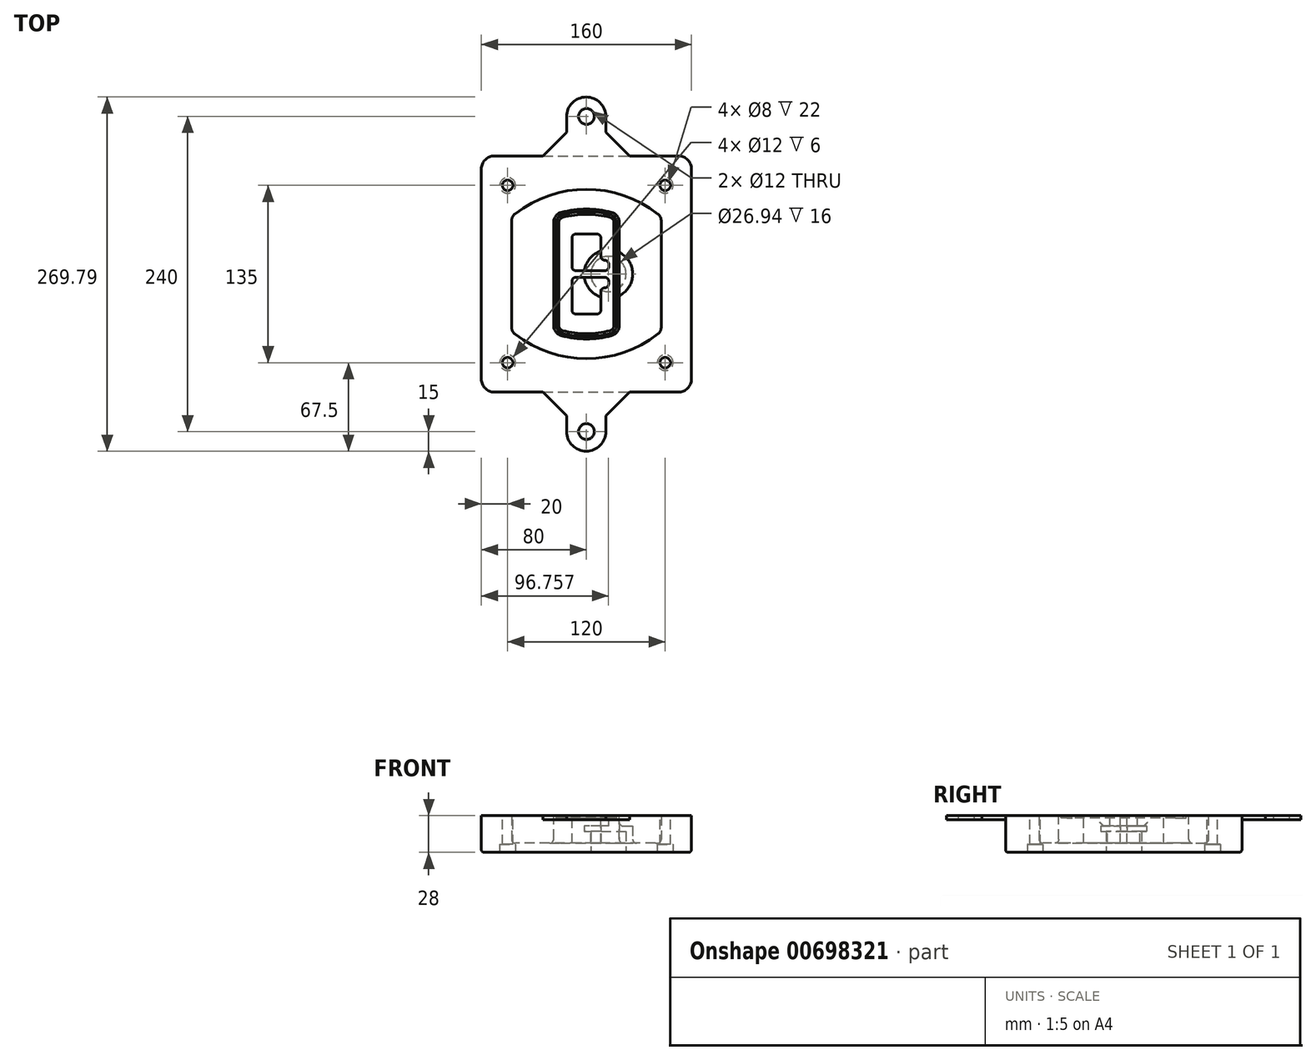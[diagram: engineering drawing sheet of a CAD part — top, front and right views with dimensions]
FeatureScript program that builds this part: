
annotation { "Feature Type Name" : "Feature", "Feature Type Description" : "" }
export const myFeature = defineFeature(function(context is Context, id is Id, definition is map)
    precondition{}
    {
        {
            var Q0;
            Q0=qCreatedBy(makeId("Top.planeOp"),FACE);
            var sketch = newSketch(context, id + "F0", { "sketchPlane" : qUnion([Q0])});
            skPoint(sketch, "E0.rect.middle", {"position": v(0, 0) * mm});
            skLineSegment(sketch, "E1.bottom", {"start": v(-70, -90) * mm, "end": v(70, -90) * mm});
            skLineSegment(sketch, "E1.top", {"start": v(-70, 90) * mm, "end": v(70, 90) * mm});
            skLineSegment(sketch, "E1.left", {"start": v(-80, -80) * mm, "end": v(-80, 80) * mm});
            skLineSegment(sketch, "E1.right", {"start": v(80, -80) * mm, "end": v(80, 80) * mm});
            skLineSegment(sketch, "E2", {"start": v(-80, 90) * mm, "end": v(80, -90) * mm, "construction": true});
            skLineSegment(sketch, "E3", {"start": v(80, 90) * mm, "end": v(-80, -90) * mm, "construction": true});
            skCircle(sketch, "E4", {"center": v(-60, 67.5) * mm, "radius": 4 * mm});
            skCircle(sketch, "E5", {"center": v(60, 67.5) * mm, "radius": 4 * mm});
            skCircle(sketch, "E6", {"center": v(60, -67.5) * mm, "radius": 4 * mm});
            skCircle(sketch, "E7", {"center": v(-60, -67.5) * mm, "radius": 4 * mm});
            skLineSegment(sketch, "E8", {"start": v(-60, 67.5) * mm, "end": v(60, 67.5) * mm, "construction": true});
            skLineSegment(sketch, "E9", {"start": v(60, 67.5) * mm, "end": v(60, -67.5) * mm, "construction": true});
            skLineSegment(sketch, "E10", {"start": v(60, -67.5) * mm, "end": v(-60, -67.5) * mm, "construction": true});
            skLineSegment(sketch, "E11", {"start": v(-60, -67.5) * mm, "end": v(-60, 67.5) * mm, "construction": true});
            skLineSegment(sketch, "E12", {"start": v(-60, 40.3) * mm, "end": v(-60, -40.3) * mm});
            skLineSegment(sketch, "E13", {"start": v(60, 40.3) * mm, "end": v(60, -40.3) * mm});
            skArc(sketch, "E14", {"start": v(56.15, 48.18) * mm, "mid": v(0, 67.5) * mm, "end": v(-56.15, 48.18) * mm});
            skArc(sketch, "E15", {"start": v(-56.15, -48.18) * mm, "mid": v(0, -67.5) * mm, "end": v(56.15, -48.18) * mm});
            skLineSegment(sketch, "E16", {"start": v(-60, 0) * mm, "end": v(60, 0) * mm, "construction": true});
            skPoint(sketch, "E17.visualSharp", {"position": v(-60, -45) * mm});
            skArc(sketch, "E17.filletArc", {"start": v(-60, -40.3) * mm, "mid": v(-58.99, -44.68) * mm, "end": v(-56.15, -48.18) * mm});
            skPoint(sketch, "E18.visualSharp", {"position": v(-60, 45) * mm});
            skArc(sketch, "E18.filletArc", {"start": v(-56.15, 48.18) * mm, "mid": v(-58.99, 44.68) * mm, "end": v(-60, 40.3) * mm});
            skPoint(sketch, "E19.visualSharp", {"position": v(60, 45) * mm});
            skArc(sketch, "E19.filletArc", {"start": v(60, 40.3) * mm, "mid": v(58.99, 44.68) * mm, "end": v(56.15, 48.18) * mm});
            skPoint(sketch, "E20.visualSharp", {"position": v(60, -45) * mm});
            skArc(sketch, "E20.filletArc", {"start": v(56.15, -48.18) * mm, "mid": v(58.99, -44.68) * mm, "end": v(60, -40.3) * mm});
            skPoint(sketch, "E21.visualSharp", {"position": v(-80, 90) * mm});
            skArc(sketch, "E21.filletArc", {"start": v(-70, 90) * mm, "mid": v(-77.07, 87.07) * mm, "end": v(-80, 80) * mm});
            skPoint(sketch, "E22.visualSharp", {"position": v(80, 90) * mm});
            skArc(sketch, "E22.filletArc", {"start": v(80, 80) * mm, "mid": v(77.07, 87.07) * mm, "end": v(70, 90) * mm});
            skPoint(sketch, "E23.visualSharp", {"position": v(80, -90) * mm});
            skArc(sketch, "E23.filletArc", {"start": v(70, -90) * mm, "mid": v(77.07, -87.07) * mm, "end": v(80, -80) * mm});
            skPoint(sketch, "E24.visualSharp", {"position": v(-80, -90) * mm});
            skArc(sketch, "E24.filletArc", {"start": v(-80, -80) * mm, "mid": v(-77.07, -87.07) * mm, "end": v(-70, -90) * mm});
            skArc(sketch, "E25.0", {"start": v(57, 40.3) * mm, "mid": v(56.3, 43.36) * mm, "end": v(54.3, 45.81) * mm});
            skLineSegment(sketch, "E25.1", {"start": v(57, 40.3) * mm, "end": v(57, -40.3) * mm});
            skArc(sketch, "E25.2", {"start": v(54.3, -45.81) * mm, "mid": v(56.3, -43.36) * mm, "end": v(57, -40.3) * mm});
            skArc(sketch, "E25.3", {"start": v(-54.3, -45.81) * mm, "mid": v(0, -64.5) * mm, "end": v(54.3, -45.81) * mm});
            skArc(sketch, "E25.4", {"start": v(-57, -40.3) * mm, "mid": v(-56.3, -43.36) * mm, "end": v(-54.3, -45.81) * mm});
            skArc(sketch, "E25.5", {"start": v(54.3, 45.81) * mm, "mid": v(0, 64.5) * mm, "end": v(-54.3, 45.81) * mm});
            skLineSegment(sketch, "E25.6", {"start": v(-57, 40.3) * mm, "end": v(-57, -40.3) * mm});
            skArc(sketch, "E25.7", {"start": v(-54.3, 45.81) * mm, "mid": v(-56.3, 43.36) * mm, "end": v(-57, 40.3) * mm});
            skArc(sketch, "E26.0", {"start": v(-58.62, 51.33) * mm, "mid": v(-62.58, 46.43) * mm, "end": v(-64, 40.3) * mm});
            skArc(sketch, "E26.1", {"start": v(58.62, 51.33) * mm, "mid": v(0, 71.5) * mm, "end": v(-58.62, 51.33) * mm});
            skArc(sketch, "E26.2", {"start": v(64, 40.3) * mm, "mid": v(62.58, 46.43) * mm, "end": v(58.62, 51.33) * mm});
            skLineSegment(sketch, "E26.3", {"start": v(64, 40.3) * mm, "end": v(64, -40.3) * mm});
            skArc(sketch, "E26.4", {"start": v(58.62, -51.33) * mm, "mid": v(62.58, -46.43) * mm, "end": v(64, -40.3) * mm});
            skLineSegment(sketch, "E26.5", {"start": v(-64, 40.3) * mm, "end": v(-64, -40.3) * mm});
            skArc(sketch, "E26.6", {"start": v(-58.62, -51.33) * mm, "mid": v(0, -71.5) * mm, "end": v(58.62, -51.33) * mm});
            skArc(sketch, "E26.7", {"start": v(-64, -40.3) * mm, "mid": v(-62.58, -46.43) * mm, "end": v(-58.62, -51.33) * mm});
            skSolve(sketch);
        }
        {
            var Q0;
            Q0=makeQuery(id+"F0.imprint","IMPRINT",FACE,{"disambiguationData":[TD([[makeQuery(id+"F0.imprint","IMPRINT",EDGE,{"derivedFrom":sQuery(id+"F0.wireOp",EDGE,"E1.bottom")}),1.0]])]});
            var Q1;
            Q1=makeQuery(id+"F0.imprint","IMPRINT",FACE,{"disambiguationData":[TD([[makeQuery(id+"F0.imprint","IMPRINT",EDGE,{"derivedFrom":sQuery(id+"F0.wireOp",EDGE,"E12")}),1.0]])]});
            var Q2;
            Q2=makeQuery(id+"F0.imprint","IMPRINT",FACE,{"disambiguationData":[TD([[makeQuery(id+"F0.imprint","IMPRINT",EDGE,{"derivedFrom":sQuery(id+"F0.wireOp",EDGE,"E25.0")}),1.0]])]});
            var Q3;
            Q3=makeQuery(id+"F0.imprint","IMPRINT",FACE,{"disambiguationData":[TD([[makeQuery(id+"F0.imprint","IMPRINT",EDGE,{"derivedFrom":sQuery(id+"F0.wireOp",EDGE,"E12")}),-1.0]])]});
            extrude(context, id + "F1", {"entities" : qUnion([Q0, Q1, Q2, Q3]), "oppositeDirection" : true, "depth" : 25 * mm, "offsetDistance" : 25 * mm});
        }
        {
            var Q0;
            Q0=makeQuery(id+"F0.imprint","IMPRINT",FACE,{"disambiguationData":[TD([[makeQuery(id+"F0.imprint","IMPRINT",EDGE,{"derivedFrom":sQuery(id+"F0.wireOp",EDGE,"E12")}),1.0]])]});
            extrude(context, id + "F2", {"entities" : qUnion([Q0]), "operationType" : NewBodyOperationType.ADD, "depth" : 3 * mm, "offsetDistance" : 25 * mm});
        }
        {
            var Q0;
            Q0=makeQuery(id+"F0.imprint","IMPRINT",FACE,{"disambiguationData":[TD([[makeQuery(id+"F0.imprint","IMPRINT",EDGE,{"derivedFrom":sQuery(id+"F0.wireOp",EDGE,"E25.0")}),1.0]])]});
            extrude(context, id + "F3", {"entities" : qUnion([Q0]), "operationType" : NewBodyOperationType.REMOVE, "oppositeDirection" : true, "depth" : 18 * mm, "offsetDistance" : 25 * mm});
        }
        {
            var Q0;
            Q0=makeQuery(id+"F2.opExtrude","CAP_FACE",FACE,{"disambiguationData":[OSD([sQuery(id+"F0.wireOp",EDGE,"E12"),sQuery(id+"F0.wireOp",EDGE,"E13"),sQuery(id+"F0.wireOp",EDGE,"E14"),sQuery(id+"F0.wireOp",EDGE,"E15"),sQuery(id+"F0.wireOp",EDGE,"E17.filletArc"),sQuery(id+"F0.wireOp",EDGE,"E18.filletArc"),sQuery(id+"F0.wireOp",EDGE,"E19.filletArc"),sQuery(id+"F0.wireOp",EDGE,"E20.filletArc"),sQuery(id+"F0.wireOp",EDGE,"E25.0"),sQuery(id+"F0.wireOp",EDGE,"E25.1"),sQuery(id+"F0.wireOp",EDGE,"E25.2"),sQuery(id+"F0.wireOp",EDGE,"E25.3"),sQuery(id+"F0.wireOp",EDGE,"E25.4"),sQuery(id+"F0.wireOp",EDGE,"E25.5"),sQuery(id+"F0.wireOp",EDGE,"E25.6"),sQuery(id+"F0.wireOp",EDGE,"E25.7")])],"isStart":false});
            var sketch = newSketch(context, id + "F4", { "sketchPlane" : qUnion([Q0])});
            skArc(sketch, "E27.0", {"start": v(-19.08, -46.97) * mm, "mid": v(0, -49.5) * mm, "end": v(19.08, -46.97) * mm});
            skArc(sketch, "E28.0", {"start": v(19.08, 46.97) * mm, "mid": v(0, 49.5) * mm, "end": v(-19.08, 46.97) * mm});
            skLineSegment(sketch, "E29", {"start": v(-25, 39.25) * mm, "end": v(-25, -39.25) * mm});
            skLineSegment(sketch, "E30", {"start": v(25, 39.25) * mm, "end": v(25, -39.25) * mm});
            skLineSegment(sketch, "E31", {"start": v(-25, 45.1) * mm, "end": v(25, 45.1) * mm, "construction": true});
            skLineSegment(sketch, "E32", {"start": v(-25, -45.1) * mm, "end": v(25, -45.1) * mm, "construction": true});
            skPoint(sketch, "E33.visualSharp", {"position": v(-25, 45.1) * mm});
            skArc(sketch, "E33.filletArc", {"start": v(-19.08, 46.97) * mm, "mid": v(-23.35, 44.11) * mm, "end": v(-25, 39.25) * mm});
            skPoint(sketch, "E34.visualSharp", {"position": v(25, 45.1) * mm});
            skArc(sketch, "E34.filletArc", {"start": v(25, 39.25) * mm, "mid": v(23.35, 44.11) * mm, "end": v(19.08, 46.97) * mm});
            skPoint(sketch, "E35.visualSharp", {"position": v(25, -45.1) * mm});
            skArc(sketch, "E35.filletArc", {"start": v(19.08, -46.97) * mm, "mid": v(23.35, -44.11) * mm, "end": v(25, -39.25) * mm});
            skPoint(sketch, "E36.visualSharp", {"position": v(-25, -45.1) * mm});
            skArc(sketch, "E36.filletArc", {"start": v(-25, -39.25) * mm, "mid": v(-23.35, -44.11) * mm, "end": v(-19.08, -46.97) * mm});
            skArc(sketch, "E37.0", {"start": v(54.3, 45.81) * mm, "mid": v(0, 64.5) * mm, "end": v(-54.3, 45.81) * mm});
            skArc(sketch, "E37.1", {"start": v(-54.3, 45.81) * mm, "mid": v(-56.3, 43.36) * mm, "end": v(-57, 40.3) * mm});
            skLineSegment(sketch, "E37.2", {"start": v(-57, 40.3) * mm, "end": v(-57, -40.3) * mm});
            skArc(sketch, "E37.3", {"start": v(-57, -40.3) * mm, "mid": v(-56.3, -43.36) * mm, "end": v(-54.3, -45.81) * mm});
            skArc(sketch, "E37.4", {"start": v(-54.3, -45.81) * mm, "mid": v(0, -64.5) * mm, "end": v(54.3, -45.81) * mm});
            skArc(sketch, "E37.5", {"start": v(54.3, -45.81) * mm, "mid": v(56.3, -43.36) * mm, "end": v(57, -40.3) * mm});
            skLineSegment(sketch, "E37.6", {"start": v(57, 40.3) * mm, "end": v(57, -40.3) * mm});
            skArc(sketch, "E37.7", {"start": v(57, 40.3) * mm, "mid": v(56.3, 43.36) * mm, "end": v(54.3, 45.81) * mm});
            skLineSegment(sketch, "E38.0", {"start": v(23, 39.25) * mm, "end": v(23, -39.25) * mm});
            skArc(sketch, "E38.1", {"start": v(18.56, -45.04) * mm, "mid": v(21.76, -42.9) * mm, "end": v(23, -39.25) * mm});
            skArc(sketch, "E38.2", {"start": v(-18.56, -45.04) * mm, "mid": v(0, -47.5) * mm, "end": v(18.56, -45.04) * mm});
            skArc(sketch, "E38.3", {"start": v(-23, -39.25) * mm, "mid": v(-21.76, -42.9) * mm, "end": v(-18.56, -45.04) * mm});
            skLineSegment(sketch, "E38.4", {"start": v(-23, 39.25) * mm, "end": v(-23, -39.25) * mm});
            skArc(sketch, "E38.5", {"start": v(23, 39.25) * mm, "mid": v(21.76, 42.9) * mm, "end": v(18.56, 45.04) * mm});
            skArc(sketch, "E38.6", {"start": v(-18.56, 45.04) * mm, "mid": v(-21.76, 42.9) * mm, "end": v(-23, 39.25) * mm});
            skArc(sketch, "E38.7", {"start": v(18.56, 45.04) * mm, "mid": v(0, 47.5) * mm, "end": v(-18.56, 45.04) * mm});
            skArc(sketch, "E39.0", {"start": v(21, 39.25) * mm, "mid": v(20.18, 41.68) * mm, "end": v(18.04, 43.1) * mm});
            skLineSegment(sketch, "E39.1", {"start": v(21, 39.25) * mm, "end": v(21, -39.25) * mm});
            skArc(sketch, "E39.2", {"start": v(18.04, -43.1) * mm, "mid": v(20.18, -41.68) * mm, "end": v(21, -39.25) * mm});
            skArc(sketch, "E39.3", {"start": v(-18.04, -43.1) * mm, "mid": v(0, -45.5) * mm, "end": v(18.04, -43.1) * mm});
            skArc(sketch, "E39.4", {"start": v(-21, -39.25) * mm, "mid": v(-20.18, -41.68) * mm, "end": v(-18.04, -43.1) * mm});
            skArc(sketch, "E39.5", {"start": v(18.04, 43.1) * mm, "mid": v(0, 45.5) * mm, "end": v(-18.04, 43.1) * mm});
            skLineSegment(sketch, "E39.6", {"start": v(-21, 39.25) * mm, "end": v(-21, -39.25) * mm});
            skArc(sketch, "E39.7", {"start": v(-18.04, 43.1) * mm, "mid": v(-20.18, 41.68) * mm, "end": v(-21, 39.25) * mm});
            skLineSegment(sketch, "E40", {"start": v(-25, 0) * mm, "end": v(25, 0) * mm, "construction": true});
            skLineSegment(sketch, "E41", {"start": v(-11, 5.5) * mm, "end": v(-11, 27.5) * mm});
            skLineSegment(sketch, "E42", {"start": v(-8, 30.5) * mm, "end": v(8, 30.5) * mm});
            skLineSegment(sketch, "E43", {"start": v(11, 27.5) * mm, "end": v(11, 13.5) * mm});
            skLineSegment(sketch, "E44", {"start": v(14, 10.5) * mm, "end": v(14, 10.5) * mm});
            skLineSegment(sketch, "E45", {"start": v(17, 7.5) * mm, "end": v(17, 5.5) * mm});
            skLineSegment(sketch, "E46", {"start": v(14, 2.5) * mm, "end": v(-8, 2.5) * mm});
            skPoint(sketch, "E47.visualSharp", {"position": v(-11, 30.5) * mm});
            skArc(sketch, "E47.filletArc", {"start": v(-8, 30.5) * mm, "mid": v(-10.12, 29.62) * mm, "end": v(-11, 27.5) * mm});
            skPoint(sketch, "E48.visualSharp", {"position": v(11, 30.5) * mm});
            skArc(sketch, "E48.filletArc", {"start": v(11, 27.5) * mm, "mid": v(10.12, 29.62) * mm, "end": v(8, 30.5) * mm});
            skPoint(sketch, "E49.visualSharp", {"position": v(11, 10.5) * mm});
            skArc(sketch, "E49.filletArc", {"start": v(11, 13.5) * mm, "mid": v(11.88, 11.38) * mm, "end": v(14, 10.5) * mm});
            skPoint(sketch, "E50.visualSharp", {"position": v(17, 10.5) * mm});
            skArc(sketch, "E50.filletArc", {"start": v(17, 7.5) * mm, "mid": v(16.12, 9.62) * mm, "end": v(14, 10.5) * mm});
            skPoint(sketch, "E51.visualSharp", {"position": v(17, 2.5) * mm});
            skArc(sketch, "E51.filletArc", {"start": v(14, 2.5) * mm, "mid": v(16.12, 3.38) * mm, "end": v(17, 5.5) * mm});
            skPoint(sketch, "E52.visualSharp", {"position": v(-11, 2.5) * mm});
            skArc(sketch, "E52.filletArc", {"start": v(-11, 5.5) * mm, "mid": v(-10.12, 3.38) * mm, "end": v(-8, 2.5) * mm});
            skLineSegment(sketch, "E53.0.MirrorCS", {"start": v(14, -2.5) * mm, "end": v(-8, -2.5) * mm});
            skArc(sketch, "E54.0.MirrorCS", {"start": v(-11, -5.5) * mm, "mid": v(-10.12, -3.38) * mm, "end": v(-8, -2.5) * mm});
            skLineSegment(sketch, "E55.0.MirrorCS", {"start": v(-11, -5.5) * mm, "end": v(-11, -27.5) * mm});
            skArc(sketch, "E56.0.MirrorCS", {"start": v(-8, -30.5) * mm, "mid": v(-10.12, -29.62) * mm, "end": v(-11, -27.5) * mm});
            skLineSegment(sketch, "E57.0.MirrorCS", {"start": v(-8, -30.5) * mm, "end": v(8, -30.5) * mm});
            skArc(sketch, "E58.0.MirrorCS", {"start": v(11, -27.5) * mm, "mid": v(10.12, -29.62) * mm, "end": v(8, -30.5) * mm});
            skLineSegment(sketch, "E59.0.MirrorCS", {"start": v(11, -27.5) * mm, "end": v(11, -13.5) * mm});
            skArc(sketch, "E60.0.MirrorCS", {"start": v(11, -13.5) * mm, "mid": v(11.88, -11.38) * mm, "end": v(14, -10.5) * mm});
            skArc(sketch, "E61.0.MirrorCS", {"start": v(17, -7.5) * mm, "mid": v(16.12, -9.62) * mm, "end": v(14, -10.5) * mm});
            skLineSegment(sketch, "E62.0.MirrorCS", {"start": v(17, -7.5) * mm, "end": v(17, -5.5) * mm});
            skArc(sketch, "E63.0.MirrorCS", {"start": v(14, -2.5) * mm, "mid": v(16.12, -3.38) * mm, "end": v(17, -5.5) * mm});
            skSolve(sketch);
        }
        {
            var Q0;
            Q0=makeQuery(id+"F4.imprint","IMPRINT",FACE,{"disambiguationData":[TD([[makeQuery(id+"F4.imprint","IMPRINT",EDGE,{"derivedFrom":sQuery(id+"F4.wireOp",EDGE,"E27.0")}),1.0]])]});
            var Q1;
            Q1=makeQuery(id+"F4.imprint","IMPRINT",FACE,{"disambiguationData":[TD([[makeQuery(id+"F4.imprint","IMPRINT",EDGE,{"derivedFrom":sQuery(id+"F4.wireOp",EDGE,"E38.0")}),-1.0]])]});
            var Q2;
            Q2=makeQuery(id+"F4.imprint","IMPRINT",FACE,{"disambiguationData":[TD([[makeQuery(id+"F4.imprint","IMPRINT",EDGE,{"derivedFrom":sQuery(id+"F4.wireOp",EDGE,"E39.0")}),1.0]])]});
            extrude(context, id + "F5", {"entities" : qUnion([Q0, Q1, Q2]), "operationType" : NewBodyOperationType.ADD, "endBound" : BoundingType.UP_TO_NEXT, "oppositeDirection" : true, "depth" : 25 * mm, "offsetDistance" : 25 * mm});
        }
        {
            var Q0;
            Q0=makeQuery(id+"F4.imprint","IMPRINT",FACE,{"disambiguationData":[TD([[makeQuery(id+"F4.imprint","IMPRINT",EDGE,{"derivedFrom":sQuery(id+"F4.wireOp",EDGE,"E38.0")}),-1.0]])]});
            extrude(context, id + "F6", {"entities" : qUnion([Q0]), "operationType" : NewBodyOperationType.REMOVE, "oppositeDirection" : true, "depth" : 2 * mm, "offsetDistance" : 25 * mm});
        }
        {
            var Q0;
            Q0=makeQuery(id+"F1.opExtrude","CAP_FACE",FACE,{"disambiguationData":[OSD([sQuery(id+"F0.wireOp",EDGE,"E1.bottom"),sQuery(id+"F0.wireOp",EDGE,"E1.top"),sQuery(id+"F0.wireOp",EDGE,"E1.left"),sQuery(id+"F0.wireOp",EDGE,"E1.right"),sQuery(id+"F0.wireOp",EDGE,"E4"),sQuery(id+"F0.wireOp",EDGE,"E5"),sQuery(id+"F0.wireOp",EDGE,"E6"),sQuery(id+"F0.wireOp",EDGE,"E7"),sQuery(id+"F0.wireOp",EDGE,"E21.filletArc"),sQuery(id+"F0.wireOp",EDGE,"E22.filletArc"),sQuery(id+"F0.wireOp",EDGE,"E23.filletArc"),sQuery(id+"F0.wireOp",EDGE,"E24.filletArc")])],"isStart":false});
            var sketch = newSketch(context, id + "F7", { "sketchPlane" : qUnion([Q0])});
            skCircle(sketch, "E64", {"center": v(16.76, 0) * mm, "radius": 13.47 * mm});
            skCircle(sketch, "E65", {"center": v(-45.56, 0) * mm, "radius": 13.47 * mm});
            skLineSegment(sketch, "E66", {"start": v(80, 0) * mm, "end": v(-80, 0) * mm});
            skCircle(sketch, "E67", {"center": v(16.76, 0) * mm, "radius": 18.47 * mm});
            skCircle(sketch, "E68", {"center": v(60, -67.5) * mm, "radius": 6 * mm});
            skCircle(sketch, "E69", {"center": v(-60, -67.5) * mm, "radius": 6 * mm});
            skCircle(sketch, "E70", {"center": v(-60, 67.5) * mm, "radius": 6 * mm});
            skCircle(sketch, "E71", {"center": v(60, 67.5) * mm, "radius": 6 * mm});
            skSolve(sketch);
        }
        {
            var Q0;
            {var subQ1=sQuery(id+"F7.wireOp",EDGE,"E66");var subQ4=sQuery(id+"F7.wireOp",EDGE,"E64");var subQ6=makeQuery(id+"F7.imprint","INTERSECT",VERTEX,{"disambiguationData":[OD(0.0)],"derivedFrom":[subQ4,subQ1]});Q0=makeQuery(id+"F7.imprint","IMPRINT",FACE,{"disambiguationData":[TD([[makeQuery(id+"F7.imprint","IMPRINT",EDGE,{"disambiguationData":[TD([[subQ6,-1.0]])],"derivedFrom":subQ4}),-1.0]])]});}
            var Q1;
            {var subQ0=sQuery(id+"F7.wireOp",EDGE,"E66");var subQ1=sQuery(id+"F7.wireOp",EDGE,"E64");var subQ3=makeQuery(id+"F7.imprint","INTERSECT",VERTEX,{"disambiguationData":[OD(0.0)],"derivedFrom":[subQ1,subQ0]});Q1=makeQuery(id+"F7.imprint","IMPRINT",FACE,{"disambiguationData":[TD([[makeQuery(id+"F7.imprint","IMPRINT",EDGE,{"disambiguationData":[TD([[subQ3,-1.0]])],"derivedFrom":subQ1}),1.0]])]});}
            var Q2;
            {var subQ0=sQuery(id+"F7.wireOp",EDGE,"E66");var subQ1=sQuery(id+"F7.wireOp",EDGE,"E64");var subQ3=makeQuery(id+"F7.imprint","INTERSECT",VERTEX,{"disambiguationData":[OD(0.0)],"derivedFrom":[subQ1,subQ0]});Q2=makeQuery(id+"F7.imprint","IMPRINT",FACE,{"disambiguationData":[TD([[makeQuery(id+"F7.imprint","IMPRINT",EDGE,{"disambiguationData":[TD([[subQ3,1.0]])],"derivedFrom":subQ1}),1.0]])]});}
            var Q3;
            {var subQ1=sQuery(id+"F7.wireOp",EDGE,"E66");var subQ4=sQuery(id+"F7.wireOp",EDGE,"E64");var subQ6=makeQuery(id+"F7.imprint","INTERSECT",VERTEX,{"disambiguationData":[OD(0.0)],"derivedFrom":[subQ4,subQ1]});Q3=makeQuery(id+"F7.imprint","IMPRINT",FACE,{"disambiguationData":[TD([[makeQuery(id+"F7.imprint","IMPRINT",EDGE,{"disambiguationData":[TD([[subQ6,1.0]])],"derivedFrom":subQ4}),-1.0]])]});}
            extrude(context, id + "F8", {"entities" : qUnion([Q0, Q1, Q2, Q3]), "operationType" : NewBodyOperationType.ADD, "oppositeDirection" : true, "depth" : 20 * mm, "offsetDistance" : 25 * mm});
        }
        {
            var Q0;
            {var subQ0=sQuery(id+"F7.wireOp",EDGE,"E66");var subQ1=sQuery(id+"F7.wireOp",EDGE,"E64");var subQ3=makeQuery(id+"F7.imprint","INTERSECT",VERTEX,{"disambiguationData":[OD(0.0)],"derivedFrom":[subQ1,subQ0]});Q0=makeQuery(id+"F7.imprint","IMPRINT",FACE,{"disambiguationData":[TD([[makeQuery(id+"F7.imprint","IMPRINT",EDGE,{"disambiguationData":[TD([[subQ3,-1.0]])],"derivedFrom":subQ1}),1.0]])]});}
            var Q1;
            {var subQ0=sQuery(id+"F7.wireOp",EDGE,"E66");var subQ1=sQuery(id+"F7.wireOp",EDGE,"E64");var subQ3=makeQuery(id+"F7.imprint","INTERSECT",VERTEX,{"disambiguationData":[OD(0.0)],"derivedFrom":[subQ1,subQ0]});Q1=makeQuery(id+"F7.imprint","IMPRINT",FACE,{"disambiguationData":[TD([[makeQuery(id+"F7.imprint","IMPRINT",EDGE,{"disambiguationData":[TD([[subQ3,1.0]])],"derivedFrom":subQ1}),1.0]])]});}
            extrude(context, id + "F9", {"entities" : qUnion([Q0, Q1]), "operationType" : NewBodyOperationType.REMOVE, "oppositeDirection" : true, "depth" : 16 * mm, "offsetDistance" : 25 * mm});
        }
        {
            var Q0;
            Q0=makeQuery(id+"F7.imprint","IMPRINT",FACE,{"disambiguationData":[TD([[makeQuery(id+"F7.imprint","IMPRINT",EDGE,{"derivedFrom":sQuery(id+"F7.wireOp",EDGE,"E68")}),1.0]])]});
            var Q1;
            Q1=makeQuery(id+"F7.imprint","IMPRINT",FACE,{"disambiguationData":[TD([[makeQuery(id+"F7.imprint","IMPRINT",EDGE,{"derivedFrom":makeQuery(id+"F1.opExtrude","CAP_EDGE",EDGE,{"disambiguationData":[OSD([sQuery(id+"F0.wireOp",EDGE,"E5")])],"isStart":false})}),-1.0]])]});
            var Q2;
            Q2=makeQuery(id+"F7.imprint","IMPRINT",FACE,{"disambiguationData":[TD([[makeQuery(id+"F7.imprint","IMPRINT",EDGE,{"derivedFrom":sQuery(id+"F7.wireOp",EDGE,"E69")}),1.0]])]});
            var Q3;
            Q3=makeQuery(id+"F7.imprint","IMPRINT",FACE,{"disambiguationData":[TD([[makeQuery(id+"F7.imprint","IMPRINT",EDGE,{"derivedFrom":makeQuery(id+"F1.opExtrude","CAP_EDGE",EDGE,{"disambiguationData":[OSD([sQuery(id+"F0.wireOp",EDGE,"E4")])],"isStart":false})}),-1.0]])]});
            var Q4;
            Q4=makeQuery(id+"F7.imprint","IMPRINT",FACE,{"disambiguationData":[TD([[makeQuery(id+"F7.imprint","IMPRINT",EDGE,{"derivedFrom":sQuery(id+"F7.wireOp",EDGE,"E70")}),1.0]])]});
            var Q5;
            Q5=makeQuery(id+"F7.imprint","IMPRINT",FACE,{"disambiguationData":[TD([[makeQuery(id+"F7.imprint","IMPRINT",EDGE,{"derivedFrom":makeQuery(id+"F1.opExtrude","CAP_EDGE",EDGE,{"disambiguationData":[OSD([sQuery(id+"F0.wireOp",EDGE,"E7")])],"isStart":false})}),-1.0]])]});
            var Q6;
            Q6=makeQuery(id+"F7.imprint","IMPRINT",FACE,{"disambiguationData":[TD([[makeQuery(id+"F7.imprint","IMPRINT",EDGE,{"derivedFrom":sQuery(id+"F7.wireOp",EDGE,"E71")}),1.0]])]});
            var Q7;
            Q7=makeQuery(id+"F7.imprint","IMPRINT",FACE,{"disambiguationData":[TD([[makeQuery(id+"F7.imprint","IMPRINT",EDGE,{"derivedFrom":makeQuery(id+"F1.opExtrude","CAP_EDGE",EDGE,{"disambiguationData":[OSD([sQuery(id+"F0.wireOp",EDGE,"E6")])],"isStart":false})}),-1.0]])]});
            extrude(context, id + "F10", {"entities" : qUnion([Q0, Q1, Q2, Q3, Q4, Q5, Q6, Q7]), "operationType" : NewBodyOperationType.REMOVE, "oppositeDirection" : true, "depth" : 6 * mm, "offsetDistance" : 25 * mm});
        }
        {
            var Q0;
            Q0=makeQuery(id+"F9.boolean.opBoolean","COPY",FACE,{"derivedFrom":makeQuery(id+"F9.opExtrude","CAP_FACE",FACE,{"disambiguationData":[OSD([sQuery(id+"F7.wireOp",EDGE,"E64")])],"isStart":false})});
            var sketch = newSketch(context, id + "F11", { "sketchPlane" : qUnion([Q0])});
            skArc(sketch, "E72.0", {"start": v(11, 17.55) * mm, "mid": v(2.57, 11.82) * mm, "end": v(-1.54, 2.5) * mm});
            skArc(sketch, "E72.1", {"start": v(-1.54, -2.5) * mm, "mid": v(2.57, -11.82) * mm, "end": v(11, -17.55) * mm});
            skLineSegment(sketch, "E73", {"start": v(-1.54, -2.5) * mm, "end": v(14, -2.5) * mm});
            skLineSegment(sketch, "E74.0", {"start": v(14, 2.5) * mm, "end": v(-1.54, 2.5) * mm});
            skArc(sketch, "E74.1", {"start": v(14, 2.5) * mm, "mid": v(16.12, 3.38) * mm, "end": v(17, 5.5) * mm});
            skLineSegment(sketch, "E74.2", {"start": v(17, 7.5) * mm, "end": v(17, 5.5) * mm});
            skArc(sketch, "E74.3", {"start": v(17, 7.5) * mm, "mid": v(16.12, 9.62) * mm, "end": v(14, 10.5) * mm});
            skArc(sketch, "E74.4", {"start": v(11, 13.5) * mm, "mid": v(11.88, 11.38) * mm, "end": v(14, 10.5) * mm});
            skLineSegment(sketch, "E74.5", {"start": v(11, 17.55) * mm, "end": v(11, 13.5) * mm});
            skLineSegment(sketch, "E74.7", {"start": v(14, -2.5) * mm, "end": v(-1.54, -2.5) * mm});
            skArc(sketch, "E74.8", {"start": v(14, -2.5) * mm, "mid": v(16.12, -3.38) * mm, "end": v(17, -5.5) * mm});
            skLineSegment(sketch, "E74.9", {"start": v(17, -7.5) * mm, "end": v(17, -5.5) * mm});
            skArc(sketch, "E74.10", {"start": v(17, -7.5) * mm, "mid": v(16.12, -9.62) * mm, "end": v(14, -10.5) * mm});
            skArc(sketch, "E74.11", {"start": v(11, -13.5) * mm, "mid": v(11.88, -11.38) * mm, "end": v(14, -10.5) * mm});
            skLineSegment(sketch, "E74.12", {"start": v(11, -17.55) * mm, "end": v(11, -13.5) * mm});
            skPoint(sketch, "E75.orphan", {"position": v(11, -27.5) * mm});
            skPoint(sketch, "E76.orphan", {"position": v(-8, -2.5) * mm});
            skPoint(sketch, "E77.orphan", {"position": v(-8, 2.5) * mm});
            skPoint(sketch, "E78.orphan", {"position": v(11, 27.5) * mm});
            skSolve(sketch);
        }
        {
            var Q0;
            {var subQ7=sQuery(id+"F11.wireOp",EDGE,"E72.0");var subQ14=sQuery(id+"F11.wireOp",EDGE,"E72.1");var subQ16=sQuery(id+"F11.wireOp",EDGE,"E74.1");var subQ18=sQuery(id+"F11.wireOp",EDGE,"E74.8");Q0=qUnion([makeQuery(id+"F11.imprint","IMPRINT",FACE,{"disambiguationData":[TD([[makeQuery(id+"F11.imprint","IMPRINT",EDGE,{"derivedFrom":subQ7}),1.0]])]}),makeQuery(id+"F11.imprint","IMPRINT",FACE,{"disambiguationData":[TD([[makeQuery(id+"F11.imprint","IMPRINT",EDGE,{"derivedFrom":subQ14}),1.0]])]}),makeQuery(id+"F11.imprint","IMPRINT",FACE,{"disambiguationData":[TD([[makeQuery(id+"F11.imprint","IMPRINT",EDGE,{"derivedFrom":subQ16}),1.0]])]}),makeQuery(id+"F11.imprint","IMPRINT",FACE,{"disambiguationData":[TD([[makeQuery(id+"F11.imprint","IMPRINT",EDGE,{"derivedFrom":subQ18}),-1.0]])]})]);}
            var Q1;
            Q1=makeQuery(id+"F5.boolean.opBoolean","SPLIT",FACE,{"disambiguationData":[TD([makeQuery(id+"F5.opExtrude","SWEPT_FACE",FACE,{"disambiguationData":[OSD([sQuery(id+"F4.wireOp",EDGE,"E41")])]})])],"derivedFrom":makeQuery(id+"F3.boolean.opBoolean","COPY",FACE,{"derivedFrom":makeQuery(id+"F3.opExtrude","CAP_FACE",FACE,{"disambiguationData":[OSD([sQuery(id+"F0.wireOp",EDGE,"E25.0"),sQuery(id+"F0.wireOp",EDGE,"E25.1"),sQuery(id+"F0.wireOp",EDGE,"E25.2"),sQuery(id+"F0.wireOp",EDGE,"E25.3"),sQuery(id+"F0.wireOp",EDGE,"E25.4"),sQuery(id+"F0.wireOp",EDGE,"E25.5"),sQuery(id+"F0.wireOp",EDGE,"E25.6"),sQuery(id+"F0.wireOp",EDGE,"E25.7")])],"isStart":false})})});
            extrude(context, id + "F12", {"entities" : qUnion([Q0]), "operationType" : NewBodyOperationType.REMOVE, "endBound" : BoundingType.UP_TO_SURFACE, "endBoundEntityFace" : qUnion([Q1]), "depth" : 25 * mm, "offsetDistance" : 25 * mm});
        }
        {
            var Q0;
            Q0=makeQuery(id+"F3.boolean.opBoolean","COPY",EDGE,{"derivedFrom":makeQuery(id+"F3.opExtrude","CAP_EDGE",EDGE,{"disambiguationData":[OSD([sQuery(id+"F0.wireOp",EDGE,"E25.6")])],"isStart":false})});
            var Q1;
            Q1=makeQuery(id+"F8.boolean.opBoolean","INTERSECT",EDGE,{"derivedFrom":[makeQuery(id+"F5.opExtrude","SWEPT_FACE",FACE,{"disambiguationData":[OSD([sQuery(id+"F4.wireOp",EDGE,"E30")])]}),makeQuery(id+"F8.opExtrude","CAP_FACE",FACE,{"disambiguationData":[OSD([sQuery(id+"F7.wireOp",EDGE,"E67")])],"isStart":false})]});
            var Q2;
            Q2=makeQuery(id+"F8.boolean.opBoolean","INTERSECT",EDGE,{"disambiguationData":[OD(1.0)],"derivedFrom":[makeQuery(id+"F5.opExtrude","SWEPT_FACE",FACE,{"disambiguationData":[OSD([sQuery(id+"F4.wireOp",EDGE,"E30")])]}),makeQuery(id+"F8.opExtrude","SWEPT_FACE",FACE,{"disambiguationData":[OSD([sQuery(id+"F7.wireOp",EDGE,"E67")])]})]});
            var Q3;
            {var subQ0=sQuery(id+"F4.wireOp",EDGE,"E30");Q3=makeQuery(id+"F8.boolean.opBoolean","SPLIT",EDGE,{"disambiguationData":[TD([makeQuery(id+"F5.opExtrude","SWEPT_FACE",FACE,{"disambiguationData":[OSD([sQuery(id+"F4.wireOp",EDGE,"E35.filletArc")])]})])],"derivedFrom":makeQuery(id+"F5.opExtrude","CAP_EDGE",EDGE,{"disambiguationData":[OSD([subQ0])],"isStart":false})});}
            var Q4;
            {var subQ0=sQuery(id+"F0.wireOp",EDGE,"E25.7");var subQ1=sQuery(id+"F0.wireOp",EDGE,"E25.1");var subQ2=sQuery(id+"F0.wireOp",EDGE,"E25.6");var subQ3=sQuery(id+"F0.wireOp",EDGE,"E25.5");var subQ4=sQuery(id+"F0.wireOp",EDGE,"E25.4");var subQ5=sQuery(id+"F0.wireOp",EDGE,"E25.0");var subQ6=sQuery(id+"F0.wireOp",EDGE,"E25.2");var subQ7=sQuery(id+"F0.wireOp",EDGE,"E25.3");Q4=makeQuery(id+"F8.boolean.opBoolean","INTERSECT",EDGE,{"derivedFrom":[makeQuery(id+"F5.boolean.opBoolean","SPLIT",FACE,{"disambiguationData":[TD([makeQuery(id+"F2.opExtrude","SWEPT_FACE",FACE,{"disambiguationData":[OSD([subQ5])]})])],"derivedFrom":makeQuery(id+"F3.boolean.opBoolean","COPY",FACE,{"derivedFrom":makeQuery(id+"F3.opExtrude","CAP_FACE",FACE,{"disambiguationData":[OSD([subQ5,subQ1,subQ6,subQ7,subQ4,subQ3,subQ2,subQ0])],"isStart":false})})}),makeQuery(id+"F8.opExtrude","SWEPT_FACE",FACE,{"disambiguationData":[OSD([sQuery(id+"F7.wireOp",EDGE,"E67")])]})]});}
            var Q5;
            Q5=makeQuery(id+"F8.boolean.opBoolean","INTERSECT",EDGE,{"disambiguationData":[OD(0.0)],"derivedFrom":[makeQuery(id+"F5.opExtrude","SWEPT_FACE",FACE,{"disambiguationData":[OSD([sQuery(id+"F4.wireOp",EDGE,"E30")])]}),makeQuery(id+"F8.opExtrude","SWEPT_FACE",FACE,{"disambiguationData":[OSD([sQuery(id+"F7.wireOp",EDGE,"E67")])]})]});
            fillet(context, id + "F13", {"entities" : qUnion([Q0, Q1, Q2, Q3, Q4, Q5]), "radius" : 3 * mm, "tangentPropagation" : true, "allowEdgeOverflow" : false});
        }
        {
            var Q0;
            Q0=makeQuery(id+"F1.opExtrude","CAP_EDGE",EDGE,{"disambiguationData":[OSD([sQuery(id+"F0.wireOp",EDGE,"E1.bottom")])],"isStart":false});
            fillet(context, id + "F14", {"entities" : qUnion([Q0]), "radius" : 2 * mm, "tangentPropagation" : true, "allowEdgeOverflow" : false});
        }
        {
            var Q0;
            {var subQ0=sQuery(id+"F0.wireOp",EDGE,"E21.filletArc");var subQ1=sQuery(id+"F0.wireOp",EDGE,"E7");var subQ2=sQuery(id+"F0.wireOp",EDGE,"E6");var subQ3=sQuery(id+"F0.wireOp",EDGE,"E5");var subQ4=sQuery(id+"F0.wireOp",EDGE,"E4");var subQ5=sQuery(id+"F0.wireOp",EDGE,"E22.filletArc");var subQ6=sQuery(id+"F0.wireOp",EDGE,"E1.bottom");var subQ7=sQuery(id+"F0.wireOp",EDGE,"E1.right");var subQ8=sQuery(id+"F0.wireOp",EDGE,"E1.top");var subQ9=sQuery(id+"F0.wireOp",EDGE,"E1.left");var subQ10=sQuery(id+"F0.wireOp",EDGE,"E23.filletArc");var subQ11=sQuery(id+"F0.wireOp",EDGE,"E24.filletArc");Q0=makeQuery(id+"F2.boolean.opBoolean","SPLIT",FACE,{"disambiguationData":[TD([makeQuery(id+"F1.opExtrude","SWEPT_FACE",FACE,{"disambiguationData":[OSD([subQ6])]})])],"derivedFrom":makeQuery(id+"F1.opExtrude","CAP_FACE",FACE,{"disambiguationData":[OSD([subQ6,subQ8,subQ9,subQ7,subQ4,subQ3,subQ2,subQ1,subQ0,subQ5,subQ10,subQ11])],"isStart":true})});}
            var sketch = newSketch(context, id + "F15", { "sketchPlane" : qUnion([Q0])});
            skLineSegment(sketch, "E79", {"start": v(0, 90) * mm, "end": v(0, 120) * mm, "construction": true});
            skCircle(sketch, "E80", {"center": v(0, 120) * mm, "radius": 6 * mm});
            skLineSegment(sketch, "E81", {"start": v(-33.1, 90) * mm, "end": v(-15.1, 108) * mm});
            skLineSegment(sketch, "E82", {"start": v(32.9, 90) * mm, "end": v(14.9, 108) * mm});
            skLineSegment(sketch, "E83", {"start": v(14.9, 108) * mm, "end": v(14.9, 119.79) * mm});
            skLineSegment(sketch, "E84", {"start": v(-15.1, 108) * mm, "end": v(-15.1, 119.79) * mm});
            skArc(sketch, "E85", {"start": v(14.9, 119.79) * mm, "mid": v(-0.1, 134.79) * mm, "end": v(-15.1, 119.79) * mm});
            skLineSegment(sketch, "E86", {"start": v(-33.1, -90) * mm, "end": v(-15.1, -108) * mm});
            skLineSegment(sketch, "E87", {"start": v(32.9, -90) * mm, "end": v(14.9, -108) * mm});
            skLineSegment(sketch, "E88", {"start": v(0, -90) * mm, "end": v(0, -120) * mm, "construction": true});
            skCircle(sketch, "E89", {"center": v(0, -120) * mm, "radius": 6 * mm});
            skLineSegment(sketch, "E90", {"start": v(-15.1, -108) * mm, "end": v(-15.1, -120) * mm});
            skLineSegment(sketch, "E91", {"start": v(14.9, -108) * mm, "end": v(14.9, -120) * mm});
            skArc(sketch, "E92", {"start": v(-15.1, -120) * mm, "mid": v(-0.1, -135) * mm, "end": v(14.9, -120) * mm});
            skSolve(sketch);
        }
        {
            var Q0;
            Q0=makeQuery(id+"F15.imprint","IMPRINT",FACE,{"disambiguationData":[TD([[makeQuery(id+"F15.imprint","IMPRINT",EDGE,{"derivedFrom":makeQuery(id+"F1.opExtrude","CAP_EDGE",EDGE,{"disambiguationData":[OSD([sQuery(id+"F0.wireOp",EDGE,"E1.left")])],"isStart":true})}),-1.0]])]});
            var Q1;
            Q1=makeQuery(id+"F2.opExtrude","CAP_FACE",FACE,{"disambiguationData":[OSD([sQuery(id+"F0.wireOp",EDGE,"E12"),sQuery(id+"F0.wireOp",EDGE,"E13"),sQuery(id+"F0.wireOp",EDGE,"E14"),sQuery(id+"F0.wireOp",EDGE,"E15"),sQuery(id+"F0.wireOp",EDGE,"E17.filletArc"),sQuery(id+"F0.wireOp",EDGE,"E18.filletArc"),sQuery(id+"F0.wireOp",EDGE,"E19.filletArc"),sQuery(id+"F0.wireOp",EDGE,"E20.filletArc"),sQuery(id+"F0.wireOp",EDGE,"E25.0"),sQuery(id+"F0.wireOp",EDGE,"E25.1"),sQuery(id+"F0.wireOp",EDGE,"E25.2"),sQuery(id+"F0.wireOp",EDGE,"E25.3"),sQuery(id+"F0.wireOp",EDGE,"E25.4"),sQuery(id+"F0.wireOp",EDGE,"E25.5"),sQuery(id+"F0.wireOp",EDGE,"E25.6"),sQuery(id+"F0.wireOp",EDGE,"E25.7")])],"isStart":false});
            extrude(context, id + "F16", {"entities" : qUnion([Q0]), "endBound" : BoundingType.UP_TO_SURFACE, "depth" : 25 * mm, "endBoundEntityFace" : qUnion([Q1]), "offsetDistance" : 25 * mm});
        }
        {
            var Q0;
            Q0=makeQuery(id+"F15.imprint","IMPRINT",FACE,{"disambiguationData":[TD([[makeQuery(id+"F15.imprint","IMPRINT",EDGE,{"derivedFrom":sQuery(id+"F15.wireOp",EDGE,"E80")}),-1.0]])]});
            var Q1;
            {var subQ1=sQuery(id+"F15.wireOp",EDGE,"E86");Q1=makeQuery(id+"F15.imprint","IMPRINT",FACE,{"disambiguationData":[TD([[makeQuery(id+"F15.imprint","IMPRINT",EDGE,{"derivedFrom":subQ1}),1.0]])]});}
            var Q2;
            Q2=makeQuery(id+"F16.opExtrude","CAP_FACE",FACE,{"disambiguationData":[OSD([sQuery(id+"F0.wireOp",EDGE,"E1.bottom"),sQuery(id+"F0.wireOp",EDGE,"E1.top"),sQuery(id+"F0.wireOp",EDGE,"E1.left"),sQuery(id+"F0.wireOp",EDGE,"E1.right"),sQuery(id+"F0.wireOp",EDGE,"E4"),sQuery(id+"F0.wireOp",EDGE,"E5"),sQuery(id+"F0.wireOp",EDGE,"E6"),sQuery(id+"F0.wireOp",EDGE,"E7"),sQuery(id+"F0.wireOp",EDGE,"E12"),sQuery(id+"F0.wireOp",EDGE,"E13"),sQuery(id+"F0.wireOp",EDGE,"E14"),sQuery(id+"F0.wireOp",EDGE,"E15"),sQuery(id+"F0.wireOp",EDGE,"E17.filletArc"),sQuery(id+"F0.wireOp",EDGE,"E18.filletArc"),sQuery(id+"F0.wireOp",EDGE,"E19.filletArc"),sQuery(id+"F0.wireOp",EDGE,"E20.filletArc"),sQuery(id+"F0.wireOp",EDGE,"E21.filletArc"),sQuery(id+"F0.wireOp",EDGE,"E22.filletArc"),sQuery(id+"F0.wireOp",EDGE,"E23.filletArc"),sQuery(id+"F0.wireOp",EDGE,"E24.filletArc")])],"isStart":false});
            extrude(context, id + "F17", {"entities" : qUnion([Q0, Q1]), "operationType" : NewBodyOperationType.ADD, "endBound" : BoundingType.UP_TO_SURFACE, "depth" : 25 * mm, "endBoundEntityFace" : qUnion([Q2]), "offsetDistance" : 25 * mm});
        }
    });
